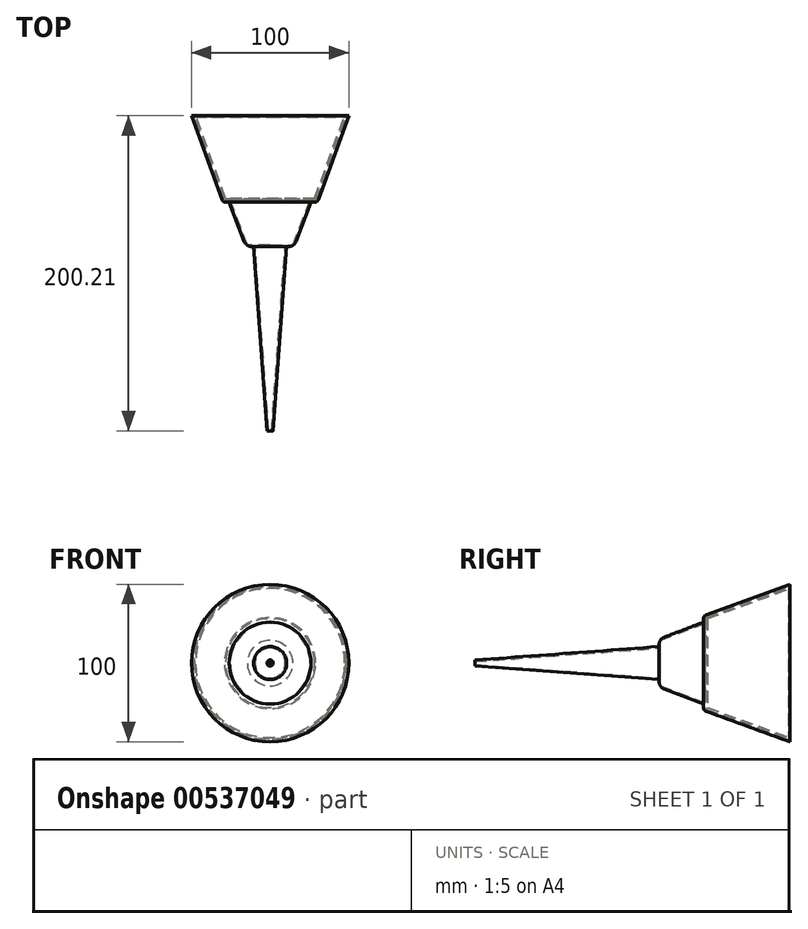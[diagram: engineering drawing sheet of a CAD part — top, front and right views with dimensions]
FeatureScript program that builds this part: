
annotation { "Feature Type Name" : "Feature", "Feature Type Description" : "" }
export const myFeature = defineFeature(function(context is Context, id is Id, definition is map)
    precondition{}
    {
        {
            var Q0;
            Q0=qCreatedBy(makeId("Top.planeOp"),FACE);
            var sketch = newSketch(context, id + "F0", { "sketchPlane" : qUnion([Q0])});
            skLineSegment(sketch, "E0", {"start": v(-30, 0) * mm, "end": v(30, 0) * mm});
            skLineSegment(sketch, "E1", {"start": v(0, 0) * mm, "end": v(0, 55) * mm});
            skLineSegment(sketch, "E2", {"start": v(-50, 55) * mm, "end": v(0, 55) * mm});
            skLineSegment(sketch, "E3", {"start": v(-50, 55) * mm, "end": v(-30, 0) * mm});
            skPoint(sketch, "E4.orphan", {"position": v(50, 55) * mm});
            skSolve(sketch);
        }
        {
            var Q0;
            {var subQ2=sQuery(id+"F0.wireOp",EDGE,"E1");Q0=makeQuery(id+"F0.imprint","IMPRINT",FACE,{"disambiguationData":[TD([[makeQuery(id+"F0.imprint","IMPRINT",EDGE,{"derivedFrom":subQ2}),1.0]])]});}
            var Q1;
            Q1=sQuery(id+"F0.wireOp",EDGE,"E1");
            revolve(context, id + "F1", {"entities" : qUnion([Q0]), "axis" : qUnion([Q1]), "revolveType" : RevolveType.FULL});
        }
        {
            var Q0;
            Q0=makeQuery(id+"F1.opRevolve","SWEPT_FACE",FACE,{"disambiguationData":[OSD([sQuery(id+"F0.wireOp",EDGE,"E2")])]});
            shell(context, id + "F2", {"entities" : qUnion([Q0]), "thickness" : 2.5 * mm});
        }
        {
            var Q0;
            Q0=qCreatedBy(makeId("Top.planeOp"),FACE);
            var sketch = newSketch(context, id + "F3", { "sketchPlane" : qUnion([Q0])});
            skLineSegment(sketch, "E5", {"start": v(50, 55) * mm, "end": v(30, 0) * mm});
            skLineSegment(sketch, "E6", {"start": v(-30, 0) * mm, "end": v(-50, 55) * mm});
            skLineSegment(sketch, "E7", {"start": v(0, 0) * mm, "end": v(0, -88.86) * mm});
            skLineSegment(sketch, "E8", {"start": v(-15.17, -28.18) * mm, "end": v(14.83, -28.18) * mm});
            skLineSegment(sketch, "E9", {"start": v(-15.17, -28.18) * mm, "end": v(-26, 0) * mm});
            skLineSegment(sketch, "E10", {"start": v(-26, 0) * mm, "end": v(0, 0) * mm});
            skSolve(sketch);
        }
        {
            var Q0;
            {var subQ4=sQuery(id+"F3.wireOp",EDGE,"E9");Q0=makeQuery(id+"F3.imprint","IMPRINT",FACE,{"disambiguationData":[TD([[makeQuery(id+"F3.imprint","IMPRINT",EDGE,{"derivedFrom":subQ4}),-1.0]])]});}
            var Q1;
            Q1=sQuery(id+"F3.wireOp",EDGE,"E7");
            revolve(context, id + "F4", {"operationType" : NewBodyOperationType.ADD, "entities" : qUnion([Q0]), "axis" : qUnion([Q1]), "revolveType" : RevolveType.FULL});
        }
        {
            var Q0;
            Q0=makeQuery(id+"F1.opRevolve","SWEPT_EDGE",EDGE,{"disambiguationData":[OSD([sQuery(id+"F0.wireOp",EDGE,"E0"),sQuery(id+"F0.wireOp",EDGE,"E3")])]});
            fillet(context, id + "F5", {"entities" : qUnion([Q0]), "radius" : 2.5 * mm, "tangentPropagation" : true, "allowEdgeOverflow" : false});
        }
        {
            var Q0;
            Q0=qCreatedBy(makeId("Top.planeOp"),FACE);
            var sketch = newSketch(context, id + "F6", { "sketchPlane" : qUnion([Q0])});
            skLineSegment(sketch, "E11.0", {"start": v(-15.17, -28.18) * mm, "end": v(15.17, -28.18) * mm});
            skLineSegment(sketch, "E12", {"start": v(0, -28.18) * mm, "end": v(0, -145.2) * mm});
            skLineSegment(sketch, "E13", {"start": v(0, -145.2) * mm, "end": v(-1.94, -145.2) * mm});
            skLineSegment(sketch, "E14", {"start": v(-1.94, -145.2) * mm, "end": v(-10.5, -28.18) * mm});
            skSolve(sketch);
        }
        {
            var Q0;
            {var subQ0=sQuery(id+"F6.wireOp",EDGE,"E12");Q0=makeQuery(id+"F6.imprint","IMPRINT",FACE,{"disambiguationData":[TD([[makeQuery(id+"F6.imprint","IMPRINT",EDGE,{"derivedFrom":subQ0}),-1.0]])]});}
            var Q1;
            Q1=sQuery(id+"F6.wireOp",EDGE,"E12");
            revolve(context, id + "F7", {"operationType" : NewBodyOperationType.ADD, "entities" : qUnion([Q0]), "axis" : qUnion([Q1]), "revolveType" : RevolveType.FULL});
        }
        {
            var Q0;
            Q0=makeQuery(id+"F7.opRevolve","SWEPT_FACE",FACE,{"disambiguationData":[OSD([sQuery(id+"F6.wireOp",EDGE,"E13")])]});
            shell(context, id + "F8", {"entities" : qUnion([Q0]), "thickness" : 1 * mm});
        }
        {
            var Q0;
            Q0=makeQuery(id+"F4.opRevolve","SWEPT_EDGE",EDGE,{"disambiguationData":[OSD([sQuery(id+"F3.wireOp",EDGE,"E8"),sQuery(id+"F3.wireOp",EDGE,"E9")])]});
            fillet(context, id + "F9", {"entities" : qUnion([Q0]), "radius" : 5 * mm, "tangentPropagation" : true, "allowEdgeOverflow" : false});
        }
    });
